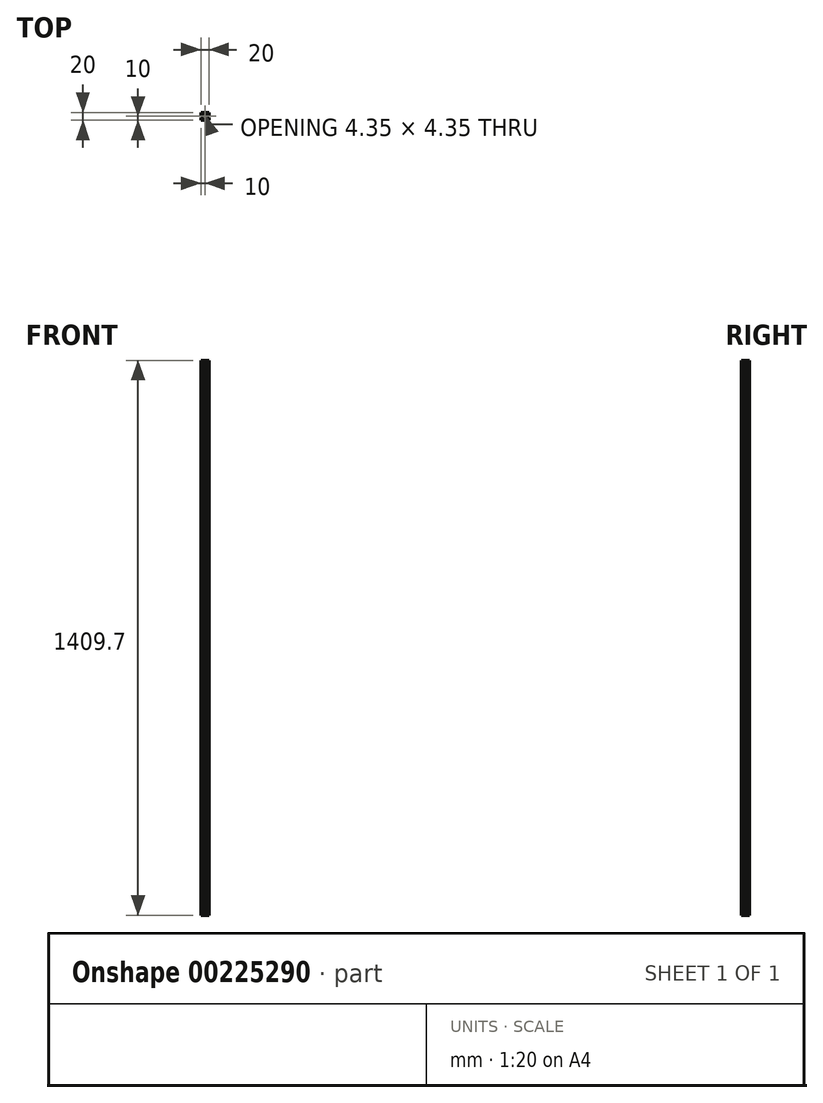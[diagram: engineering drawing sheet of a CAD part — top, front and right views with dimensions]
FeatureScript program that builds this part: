
annotation { "Feature Type Name" : "Feature", "Feature Type Description" : "" }
export const myFeature = defineFeature(function(context is Context, id is Id, definition is map)
    precondition{}
    {
        {
            var Q0;
            Q0=qCreatedBy(makeId("Top.planeOp"),FACE);
            var sketch = newSketch(context, id + "F0", { "sketchPlane" : qUnion([Q0])});
            skLineSegment(sketch, "E0.bottom", {"start": v(10, 10) * mm, "end": v(-10, 10) * mm});
            skLineSegment(sketch, "E0.top", {"start": v(10, -10) * mm, "end": v(-10, -10) * mm});
            skLineSegment(sketch, "E0.left", {"start": v(10, 10) * mm, "end": v(10, -10) * mm});
            skLineSegment(sketch, "E0.right", {"start": v(-10, 10) * mm, "end": v(-10, -10) * mm});
            skPoint(sketch, "E0.middle", {"position": v(0, 0) * mm});
            skLineSegment(sketch, "E1", {"start": v(-10, 10) * mm, "end": v(10, -10) * mm, "construction": true});
            skLineSegment(sketch, "E2", {"start": v(-10, -10) * mm, "end": v(10, 10) * mm, "construction": true});
            skLineSegment(sketch, "E3", {"start": v(0, 10) * mm, "end": v(0, -10) * mm, "construction": true});
            skLineSegment(sketch, "E4", {"start": v(-10, 0) * mm, "end": v(10, 0) * mm, "construction": true});
            skPoint(sketch, "E4.endSnap0", {"position": v(10, 0) * mm});
            skLineSegment(sketch, "E5", {"start": v(-2.63, 13.49) * mm, "end": v(2.63, 13.49) * mm});
            skLineSegment(sketch, "E6", {"start": v(2.63, 13.49) * mm, "end": v(2.63, 8.5) * mm});
            skLineSegment(sketch, "E7", {"start": v(2.63, 8.5) * mm, "end": v(6, 8.5) * mm});
            skLineSegment(sketch, "E8", {"start": v(6, 8.5) * mm, "end": v(6, 7.06) * mm});
            skLineSegment(sketch, "E9", {"start": v(6, 7.06) * mm, "end": v(2.6, 3.66) * mm});
            skLineSegment(sketch, "E10", {"start": v(2.6, 3.66) * mm, "end": v(-2.6, 3.66) * mm});
            skLineSegment(sketch, "E11", {"start": v(-2.6, 3.66) * mm, "end": v(-6, 7.06) * mm});
            skLineSegment(sketch, "E12", {"start": v(-6, 7.06) * mm, "end": v(-6, 8.5) * mm});
            skLineSegment(sketch, "E13", {"start": v(-6, 8.5) * mm, "end": v(-2.63, 8.5) * mm});
            skLineSegment(sketch, "E14", {"start": v(-2.63, 8.5) * mm, "end": v(-2.63, 13.49) * mm});
            skCircle(sketch, "E15", {"center": v(0, 0) * mm, "radius": 2.1 * mm});
            skLineSegment(sketch, "E16.MirrorCS", {"start": v(-7.06, 6) * mm, "end": v(-8.5, 6) * mm});
            skLineSegment(sketch, "E17.MirrorCS", {"start": v(-3.66, 2.6) * mm, "end": v(-7.06, 6) * mm});
            skLineSegment(sketch, "E18.MirrorCS", {"start": v(-8.5, 6) * mm, "end": v(-8.5, 2.63) * mm});
            skLineSegment(sketch, "E19.MirrorCS", {"start": v(-3.66, -2.6) * mm, "end": v(-3.66, 2.6) * mm});
            skLineSegment(sketch, "E20.MirrorCS", {"start": v(-7.06, -6) * mm, "end": v(-3.66, -2.6) * mm});
            skLineSegment(sketch, "E21.MirrorCS", {"start": v(-8.5, -6) * mm, "end": v(-7.06, -6) * mm});
            skLineSegment(sketch, "E22.MirrorCS", {"start": v(-8.5, -2.63) * mm, "end": v(-8.5, -6) * mm});
            skLineSegment(sketch, "E23.MirrorCS", {"start": v(-13.49, -2.63) * mm, "end": v(-8.5, -2.63) * mm});
            skLineSegment(sketch, "E24.MirrorCS", {"start": v(-13.49, 2.63) * mm, "end": v(-13.49, -2.63) * mm});
            skLineSegment(sketch, "E25.MirrorCS", {"start": v(-8.5, 2.63) * mm, "end": v(-13.49, 2.63) * mm});
            skLineSegment(sketch, "E26.MirrorCS", {"start": v(-2.6, -3.66) * mm, "end": v(-6, -7.06) * mm});
            skLineSegment(sketch, "E27.MirrorCS", {"start": v(2.6, -3.66) * mm, "end": v(-2.6, -3.66) * mm});
            skLineSegment(sketch, "E28.MirrorCS", {"start": v(6, -7.06) * mm, "end": v(2.6, -3.66) * mm});
            skLineSegment(sketch, "E29.MirrorCS", {"start": v(6, -8.5) * mm, "end": v(6, -7.06) * mm});
            skLineSegment(sketch, "E30.MirrorCS", {"start": v(2.63, -8.5) * mm, "end": v(6, -8.5) * mm});
            skLineSegment(sketch, "E31.MirrorCS", {"start": v(2.63, -13.49) * mm, "end": v(2.63, -8.5) * mm});
            skLineSegment(sketch, "E32.MirrorCS", {"start": v(-2.63, -13.49) * mm, "end": v(2.63, -13.49) * mm});
            skLineSegment(sketch, "E33.MirrorCS", {"start": v(-2.63, -8.5) * mm, "end": v(-2.63, -13.49) * mm});
            skLineSegment(sketch, "E34.MirrorCS", {"start": v(-6, -8.5) * mm, "end": v(-2.63, -8.5) * mm});
            skLineSegment(sketch, "E35.MirrorCS", {"start": v(-6, -7.06) * mm, "end": v(-6, -8.5) * mm});
            skLineSegment(sketch, "E36.MirrorCS", {"start": v(7.06, 6) * mm, "end": v(3.66, 2.6) * mm});
            skLineSegment(sketch, "E37.MirrorCS", {"start": v(8.5, 6) * mm, "end": v(7.06, 6) * mm});
            skLineSegment(sketch, "E38.MirrorCS", {"start": v(8.5, 2.63) * mm, "end": v(8.5, 6) * mm});
            skLineSegment(sketch, "E39.MirrorCS", {"start": v(13.49, 2.63) * mm, "end": v(8.5, 2.63) * mm});
            skLineSegment(sketch, "E40.MirrorCS", {"start": v(13.49, -2.63) * mm, "end": v(13.49, 2.63) * mm});
            skLineSegment(sketch, "E41.MirrorCS", {"start": v(8.5, -2.63) * mm, "end": v(13.49, -2.63) * mm});
            skLineSegment(sketch, "E42.MirrorCS", {"start": v(8.5, -6) * mm, "end": v(8.5, -2.63) * mm});
            skLineSegment(sketch, "E43.MirrorCS", {"start": v(7.06, -6) * mm, "end": v(8.5, -6) * mm});
            skLineSegment(sketch, "E44.MirrorCS", {"start": v(3.66, -2.6) * mm, "end": v(7.06, -6) * mm});
            skLineSegment(sketch, "E45.MirrorCS", {"start": v(3.66, 2.6) * mm, "end": v(3.66, -2.6) * mm});
            skCircle(sketch, "E46", {"center": v(-1.48, 1.48) * mm, "radius": 0.7 * mm});
            skCircle(sketch, "E47.MirrorC", {"center": v(1.48, 1.48) * mm, "radius": 0.7 * mm});
            skCircle(sketch, "E48.MirrorC", {"center": v(-1.48, -1.48) * mm, "radius": 0.7 * mm});
            skCircle(sketch, "E49.MirrorC", {"center": v(1.48, -1.48) * mm, "radius": 0.7 * mm});
            skSolve(sketch);
        }
        {
            var Q0;
            {var subQ29=sQuery(id+"F0.wireOp",EDGE,"E7");Q0=makeQuery(id+"F0.imprint","IMPRINT",FACE,{"disambiguationData":[TD([[makeQuery(id+"F0.imprint","IMPRINT",EDGE,{"derivedFrom":subQ29}),1.0]])]});}
            extrude(context, id + "F1", {"entities" : qUnion([Q0]), "depth" : 1409.7 * mm});
        }
    });
